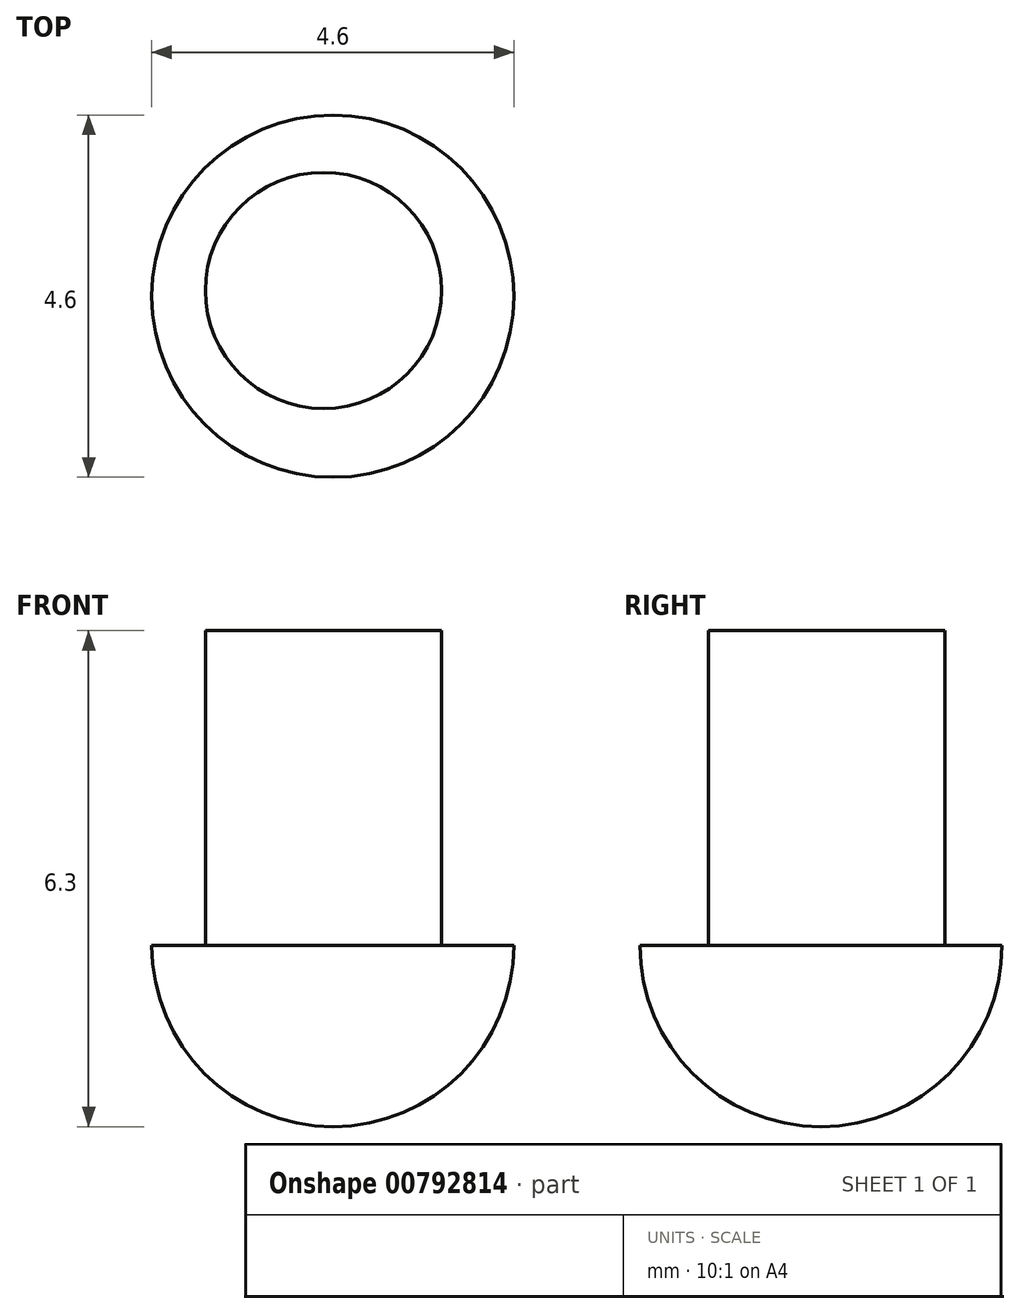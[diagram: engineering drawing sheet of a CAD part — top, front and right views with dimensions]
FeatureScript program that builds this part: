
annotation { "Feature Type Name" : "Feature", "Feature Type Description" : "" }
export const myFeature = defineFeature(function(context is Context, id is Id, definition is map)
    precondition{}
    {
        {
            var Q0;
            Q0=qCreatedBy(makeId("Front.planeOp"),FACE);
            var sketch = newSketch(context, id + "F0", { "sketchPlane" : qUnion([Q0])});
            skArc(sketch, "E0", {"start": v(2.3, 0) * mm, "mid": v(0, 2.3) * mm, "end": v(-2.3, 0) * mm});
            skLineSegment(sketch, "E1", {"start": v(-2.3, 0) * mm, "end": v(2.3, 0) * mm});
            skSolve(sketch);
        }
        {
            var Q0;
            Q0=makeQuery(id+"F0.imprint","IMPRINT",FACE,{"disambiguationData":[TD([[makeQuery(id+"F0.imprint","IMPRINT",EDGE,{"derivedFrom":sQuery(id+"F0.wireOp",EDGE,"E0")}),1.0]])]});
            var Q1;
            Q1=sQuery(id+"F0.wireOp",EDGE,"E1");
            revolve(context, id + "F1", {"surfaceOperationType" : NewSurfaceOperationType.NEW, "entities" : qUnion([Q0]), "axis" : qUnion([Q1]), "revolveType" : RevolveType.FULL});
        }
        {
            var Q0;
            Q0=qCreatedBy(makeId("Front.planeOp"),FACE);
            cPlane(context, id + "F2", {"entities" : qUnion([Q0]), "cplaneType" : CPlaneType.OFFSET, "offset" : 10 * mm, "width" : 150 * mm, "height" : 150 * mm});
        }
        {
            var Q0;
            Q0=qCreatedBy(id+"F2.planeOp",FACE);
            var sketch = newSketch(context, id + "F3", { "sketchPlane" : qUnion([Q0])});
            skLineSegment(sketch, "E2", {"start": v(-4.35, 0) * mm, "end": v(5.65, 0) * mm});
            skLineSegment(sketch, "E3", {"start": v(5.65, 0) * mm, "end": v(5.65, 4.65) * mm});
            skLineSegment(sketch, "E4", {"start": v(5.65, 4.65) * mm, "end": v(-4.35, 4.65) * mm});
            skLineSegment(sketch, "E5", {"start": v(-4.35, 4.65) * mm, "end": v(-4.35, 0) * mm});
            skSolve(sketch);
        }
        {
            var Q0;
            Q0 = qSketchRegion(id + "F3", true);
            extrude(context, id + "F4", {"entities" : qUnion([Q0]), "operationType" : NewBodyOperationType.REMOVE, "oppositeDirection" : true, "depth" : 25 * mm, "offsetDistance" : 25 * mm});
        }
        {
            var Q0;
            Q0=makeQuery(id+"F4.boolean.opBoolean","COPY",FACE,{"derivedFrom":makeQuery(id+"F4.opExtrude","SWEPT_FACE",FACE,{"disambiguationData":[OSD([sQuery(id+"F3.wireOp",EDGE,"E2")])]})});
            var sketch = newSketch(context, id + "F5", { "sketchPlane" : qUnion([Q0])});
            skCircle(sketch, "E6", {"center": v(-0.12, 0.07) * mm, "radius": 1.5 * mm});
            skSolve(sketch);
        }
        {
            var Q0;
            Q0 = qSketchRegion(id + "F5", true);
            extrude(context, id + "F6", {"entities" : qUnion([Q0]), "operationType" : NewBodyOperationType.ADD, "depth" : 4 * mm, "offsetDistance" : 25 * mm});
        }
    });
